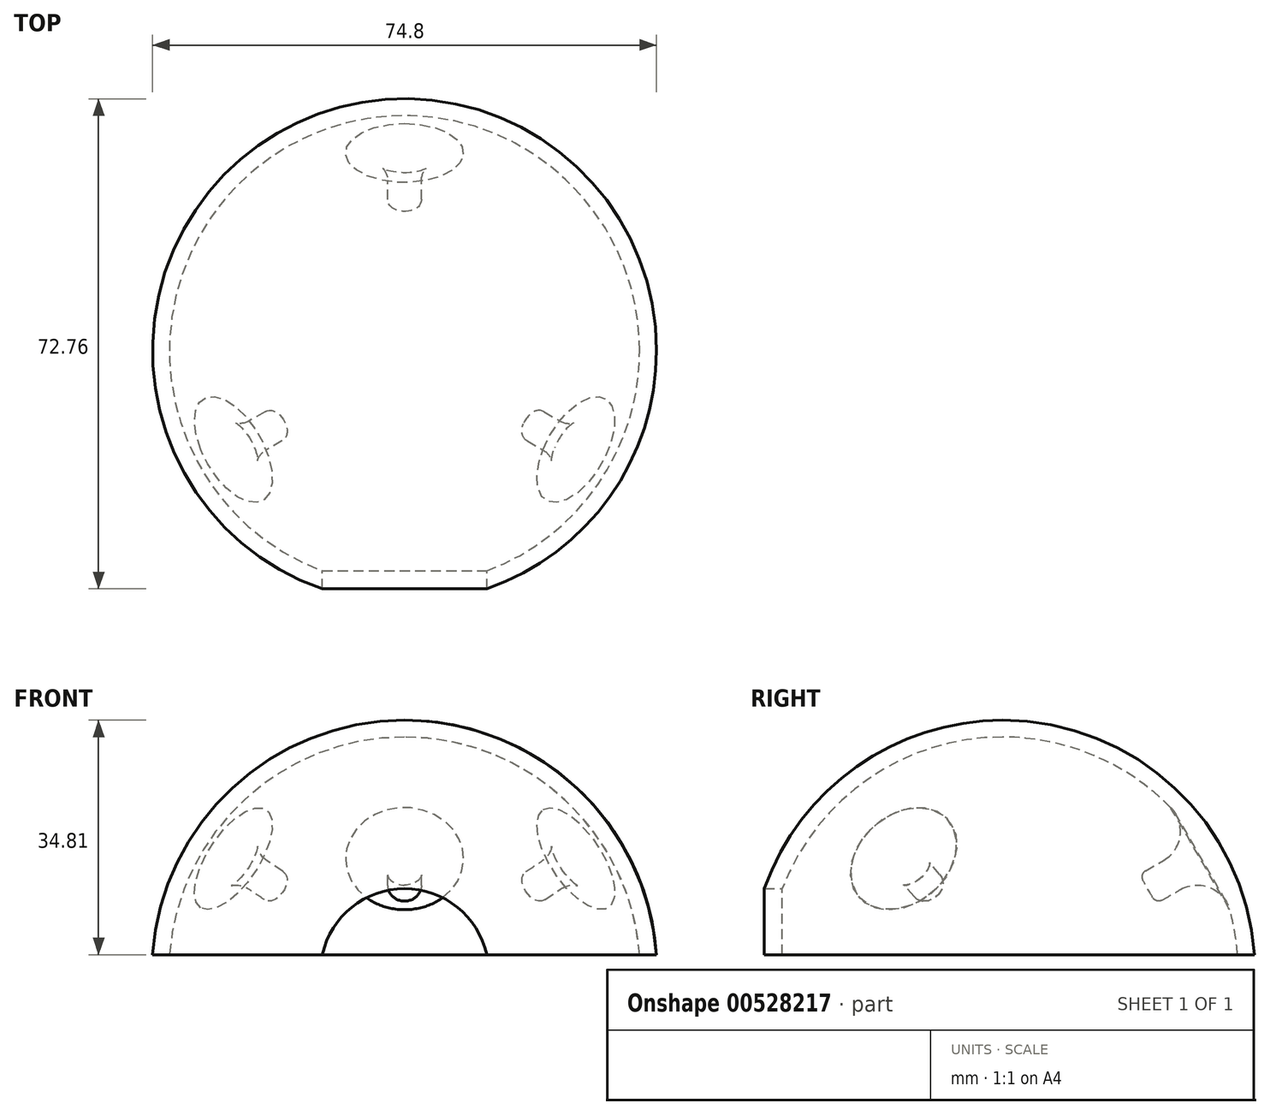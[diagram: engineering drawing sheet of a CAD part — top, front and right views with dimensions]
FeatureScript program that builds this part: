
annotation { "Feature Type Name" : "Feature", "Feature Type Description" : "" }
export const myFeature = defineFeature(function(context is Context, id is Id, definition is map)
    precondition{}
    {
        {
            var Q0;
            Q0=qCreatedBy(makeId("Front.planeOp"),FACE);
            var sketch = newSketch(context, id + "F0", { "sketchPlane" : qUnion([Q0])});
            skArc(sketch, "E0", {"start": v(37.4, 2.7) * mm, "mid": v(25.55, 27.45) * mm, "end": v(0, 37.5) * mm});
            skArc(sketch, "E1", {"start": v(34.9, 2.7) * mm, "mid": v(23.78, 25.68) * mm, "end": v(0, 35) * mm});
            skLineSegment(sketch, "E2", {"start": v(0, 37.5) * mm, "end": v(0, 35) * mm});
            skLineSegment(sketch, "E3.top", {"start": v(37.4, 2.7) * mm, "end": v(34.9, 2.7) * mm});
            skSolve(sketch);
        }
        {
            var Q0;
            Q0=makeQuery(id+"F0.imprint","IMPRINT",FACE,{"disambiguationData":[TD([[makeQuery(id+"F0.imprint","IMPRINT",EDGE,{"derivedFrom":sQuery(id+"F0.wireOp",EDGE,"E0")}),1.0]])]});
            var Q1;
            Q1=sQuery(id+"F0.wireOp",EDGE,"E2");
            revolve(context, id + "F1", {"entities" : qUnion([Q0]), "axis" : qUnion([Q1]), "revolveType" : RevolveType.FULL});
        }
        {
            var Q0;
            Q0=qCreatedBy(makeId("Front.planeOp"),FACE);
            var sketch = newSketch(context, id + "F2", { "sketchPlane" : qUnion([Q0])});
            skCircle(sketch, "E4", {"center": v(0, 0) * mm, "radius": 12.5 * mm});
            skSolve(sketch);
        }
        {
            var Q0;
            Q0 = qSketchRegion(id + "F2", true);
            extrude(context, id + "F3", {"entities" : qUnion([Q0]), "operationType" : NewBodyOperationType.REMOVE, "endBound" : BoundingType.THROUGH_ALL, "depth" : 25 * mm, "offsetDistance" : 25 * mm});
        }
        {
            var Q0;
            Q0=makeQuery(id+"F1.opRevolve","SWEPT_EDGE",EDGE,{"disambiguationData":[OSD([sQuery(id+"F0.wireOp",EDGE,"E1"),sQuery(id+"F0.wireOp",EDGE,"E3.top")])]});
            cPoint(context, id + "F4", {"entities" : qUnion([Q0]), "parameter" : 0.5});
        }
        {
            var Q0;
            Q0=qCreatedBy(makeId("Front.planeOp"),FACE);
            var Q1;
            Q1 = qCreatedBy(id + "F4" ,VERTEX);
            cPlane(context, id + "F5", {"entities" : qUnion([Q0, Q1]), "cplaneType" : CPlaneType.PLANE_POINT, "offset" : 25 * mm, "width" : 150 * mm, "height" : 150 * mm});
        }
        {
            var Q0;
            Q0=qCreatedBy(id+"F5.planeOp",FACE);
            var sketch = newSketch(context, id + "F6", { "sketchPlane" : qUnion([Q0])});
            skCircle(sketch, "E5", {"center": v(0, 0) * mm, "radius": 2.5 * mm});
            skSolve(sketch);
        }
        {
            var Q0;
            Q0=qCreatedBy(makeId("Top.planeOp"),FACE);
            var sketch = newSketch(context, id + "F7", { "sketchPlane" : qUnion([Q0])});
            skLineSegment(sketch, "E6", {"start": v(-46.34, 0) * mm, "end": v(50.33, 0) * mm, "construction": true});
            skSolve(sketch);
        }
        {
            var Q0;
            Q0 = qSketchRegion(id + "F6", true);
            extrude(context, id + "F8", {"entities" : qUnion([Q0]), "operationType" : NewBodyOperationType.ADD, "depth" : 10 * mm, "offsetDistance" : 25 * mm, "hasSecondDirection" : true, "secondDirectionOppositeDirection" : true, "secondDirectionDepth" : 1 * mm});
        }
        {
            var Q0;
            Q0=makeQuery(id+"F8.opExtrude","SWEPT_BODY",BODY,{"disambiguationData":[OSD([sQuery(id+"F6.wireOp",EDGE,"E5")])]});
            var Q1;
            Q1=sQuery(id+"F7.wireOp",EDGE,"E6");
            transform(context, id + "F9", {"entities" : qUnion([Q0]), "transformType" : TransformType.ROTATION, "transformAxis" : qUnion([Q1]), "angle" : 30 * degree, "makeCopy" : false});
        }
        {
            var Q0;
            Q0=qCreatedBy(makeId("Front.planeOp"),FACE);
            var sketch = newSketch(context, id + "F10", { "sketchPlane" : qUnion([Q0])});
            skLineSegment(sketch, "E7", {"start": v(0, 0) * mm, "end": v(0, 49.93) * mm, "construction": true});
            skSolve(sketch);
        }
        {
            var Q0;
            Q0=makeQuery(id+"F8.opExtrude","SWEPT_BODY",BODY,{"disambiguationData":[OSD([sQuery(id+"F6.wireOp",EDGE,"E5")])]});
            var Q1;
            Q1=sQuery(id+"F10.wireOp",EDGE,"E7");
            circularPattern(context, id + "F11", {"operationType" : NewBodyOperationType.ADD, "entities" : qUnion([Q0]), "axis" : qUnion([Q1]), "angle" : 360 * degree, "instanceCount" : 3, "equalSpace" : true});
        }
        {
            var Q0;
            Q0=makeQuery(id+"F11.boolean.opBoolean","INTERSECT",EDGE,{"derivedFrom":[makeQuery(id+"F1.opRevolve","SWEPT_FACE",FACE,{"disambiguationData":[OSD([sQuery(id+"F0.wireOp",EDGE,"E1")])]}),makeQuery(id+"F11.opPattern","COPY",FACE,{"derivedFrom":makeQuery(id+"F8.opExtrude","SWEPT_FACE",FACE,{"disambiguationData":[OSD([sQuery(id+"F6.wireOp",EDGE,"E5")])]}),"instanceName":"2"})]});
            var Q1;
            Q1=makeQuery(id+"F11.boolean.opBoolean","INTERSECT",EDGE,{"derivedFrom":[makeQuery(id+"F1.opRevolve","SWEPT_FACE",FACE,{"disambiguationData":[OSD([sQuery(id+"F0.wireOp",EDGE,"E1")])]}),makeQuery(id+"F8.opExtrude","SWEPT_FACE",FACE,{"disambiguationData":[OSD([sQuery(id+"F6.wireOp",EDGE,"E5")])]})]});
            var Q2;
            Q2=makeQuery(id+"F11.boolean.opBoolean","INTERSECT",EDGE,{"derivedFrom":[makeQuery(id+"F1.opRevolve","SWEPT_FACE",FACE,{"disambiguationData":[OSD([sQuery(id+"F0.wireOp",EDGE,"E1")])]}),makeQuery(id+"F11.opPattern","COPY",FACE,{"derivedFrom":makeQuery(id+"F8.opExtrude","SWEPT_FACE",FACE,{"disambiguationData":[OSD([sQuery(id+"F6.wireOp",EDGE,"E5")])]}),"instanceName":"1"})]});
            fillet(context, id + "F12", {"entities" : qUnion([Q0, Q1, Q2]), "radius" : 5 * mm, "tangentPropagation" : true, "allowEdgeOverflow" : false});
        }
        {
            var Q0;
            Q0=makeQuery(id+"F11.opPattern","COPY",EDGE,{"derivedFrom":makeQuery(id+"F8.opExtrude","CAP_EDGE",EDGE,{"disambiguationData":[OSD([sQuery(id+"F6.wireOp",EDGE,"E5")])],"isStart":false}),"instanceName":"1"});
            var Q1;
            Q1=makeQuery(id+"F11.opPattern","COPY",EDGE,{"derivedFrom":makeQuery(id+"F8.opExtrude","CAP_EDGE",EDGE,{"disambiguationData":[OSD([sQuery(id+"F6.wireOp",EDGE,"E5")])],"isStart":false}),"instanceName":"2"});
            var Q2;
            Q2=makeQuery(id+"F8.opExtrude","CAP_EDGE",EDGE,{"disambiguationData":[OSD([sQuery(id+"F6.wireOp",EDGE,"E5")])],"isStart":false});
            fillet(context, id + "F13", {"entities" : qUnion([Q0, Q1, Q2]), "radius" : 1 * mm, "tangentPropagation" : true, "allowEdgeOverflow" : false});
        }
    });
